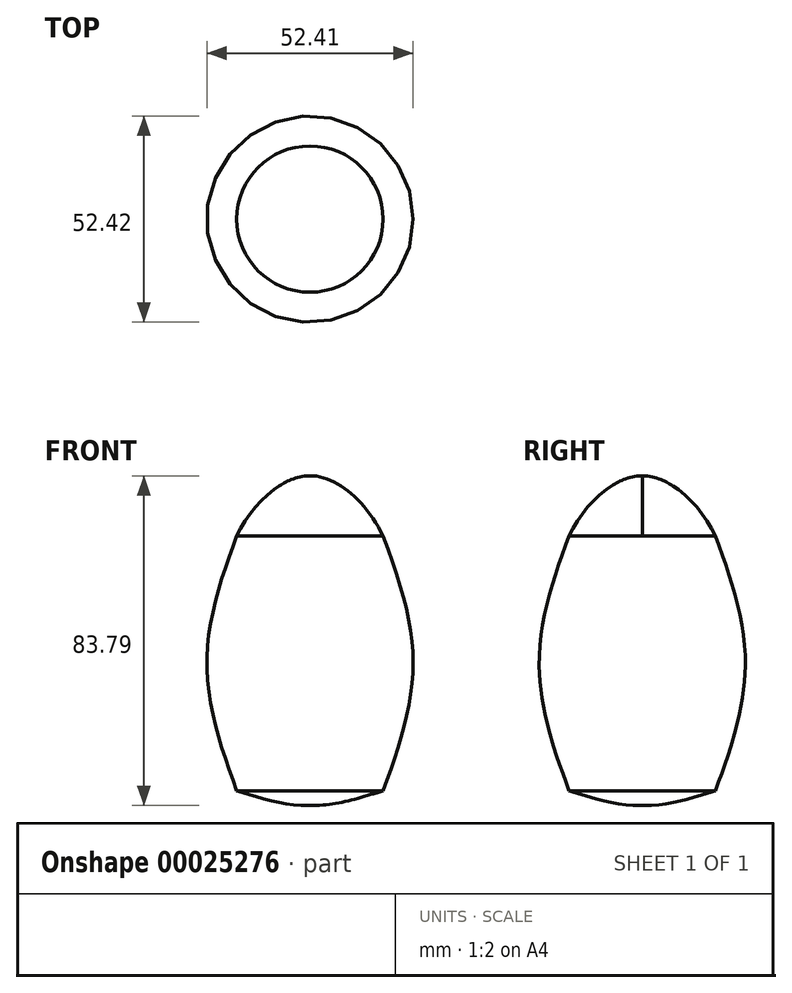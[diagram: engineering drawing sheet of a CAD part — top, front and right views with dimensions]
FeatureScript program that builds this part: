
annotation { "Feature Type Name" : "Feature", "Feature Type Description" : "" }
export const myFeature = defineFeature(function(context is Context, id is Id, definition is map)
    precondition{}
    {
        {
            var Q0;
            Q0=qCreatedBy(makeId("Front.planeOp"),FACE);
            var sketch = newSketch(context, id + "F0", { "sketchPlane" : qUnion([Q0])});
            skFitSpline(sketch, "E0", {"points": [v(-20.46, -29.32) * mm, v(-25.03, 0) * mm, v(-16.03, 34.42) * mm], "startDerivative": vector(-14.28, 60.06) * mm, "endDerivative": vector(33.5, 71.64) * mm});
            skFitSpline(sketch, "E1", {"points": [v(-16.03, 34.42) * mm, v(0, 49.67) * mm, v(18.58, 34.42) * mm], "startDerivative": vector(29.6, 55.5) * mm, "endDerivative": vector(25.98, -53.25) * mm});
            skFitSpline(sketch, "E2", {"points": [v(18.58, 34.42) * mm, v(26.16, 0) * mm, v(18.58, -30.34) * mm], "startDerivative": vector(29.37, -78.57) * mm, "endDerivative": vector(-23.12, -61.9) * mm});
            skFitSpline(sketch, "E3", {"points": [v(-20.46, -29.32) * mm, v(0, -34.1) * mm, v(18.58, -30.34) * mm], "startDerivative": vector(40.34, -13.7) * mm, "endDerivative": vector(37.71, 11.89) * mm});
            skLineSegment(sketch, "E4", {"start": v(0, 61.43) * mm, "end": v(0, -45.7) * mm});
            skSolve(sketch);
        }
        {
            var Q0;
            {var subQ5=sQuery(id+"F0.wireOp",EDGE,"E2");Q0=makeQuery(id+"F0.imprint","IMPRINT",FACE,{"disambiguationData":[TD([[makeQuery(id+"F0.imprint","IMPRINT",EDGE,{"derivedFrom":subQ5}),-1.0]])]});}
            var Q1;
            Q1=sQuery(id+"F0.wireOp",EDGE,"E4");
            revolve(context, id + "F1", {"entities" : qUnion([Q0]), "axis" : qUnion([Q1]), "revolveType" : RevolveType.FULL});
        }
    });
